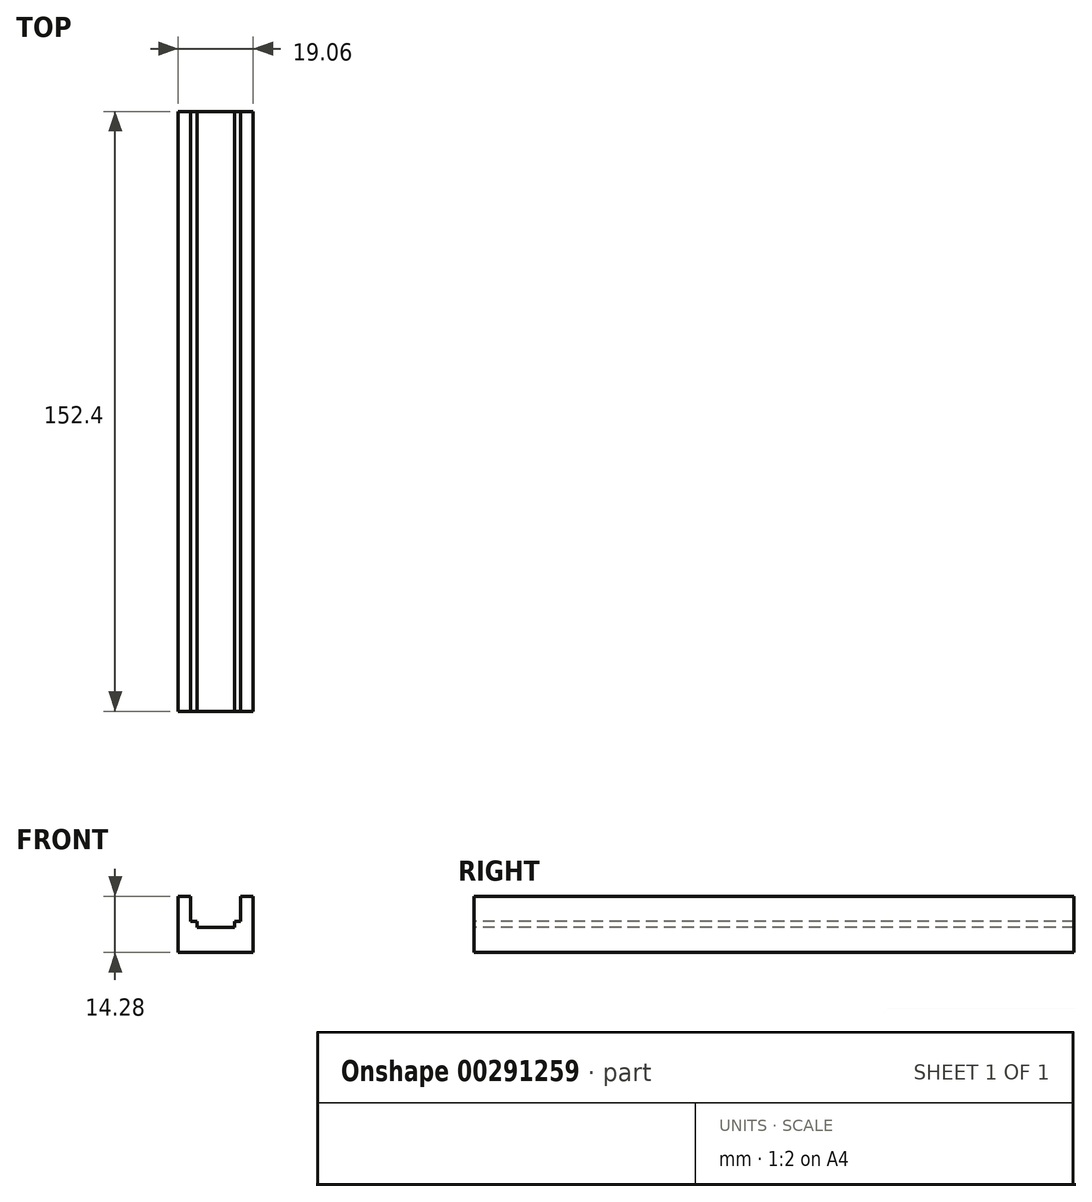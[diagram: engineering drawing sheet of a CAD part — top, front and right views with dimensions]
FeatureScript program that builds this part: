
annotation { "Feature Type Name" : "Feature", "Feature Type Description" : "" }
export const myFeature = defineFeature(function(context is Context, id is Id, definition is map)
    precondition{}
    {
        {
            var Q0;
            Q0=qCreatedBy(makeId("Front.planeOp"),FACE);
            var sketch = newSketch(context, id + "F0", { "sketchPlane" : qUnion([Q0])});
            skLineSegment(sketch, "E0", {"start": v(-4.76, 0) * mm, "end": v(4.76, 0) * mm});
            skLineSegment(sketch, "E1", {"start": v(4.76, 0) * mm, "end": v(4.76, 1.52) * mm});
            skLineSegment(sketch, "E2", {"start": v(4.76, 1.52) * mm, "end": v(6.35, 1.52) * mm});
            skLineSegment(sketch, "E3", {"start": v(6.35, 1.52) * mm, "end": v(6.35, 7.87) * mm});
            skLineSegment(sketch, "E4", {"start": v(6.35, 7.87) * mm, "end": v(9.53, 7.87) * mm});
            skLineSegment(sketch, "E5", {"start": v(9.53, 7.87) * mm, "end": v(9.53, -6.41) * mm});
            skLineSegment(sketch, "E6", {"start": v(9.53, -6.41) * mm, "end": v(-9.53, -6.41) * mm});
            skLineSegment(sketch, "E7", {"start": v(-9.53, -6.41) * mm, "end": v(-9.53, 7.87) * mm});
            skLineSegment(sketch, "E8", {"start": v(-9.53, 7.87) * mm, "end": v(-6.35, 7.87) * mm});
            skLineSegment(sketch, "E9", {"start": v(-6.35, 7.87) * mm, "end": v(-6.35, 1.52) * mm});
            skLineSegment(sketch, "E10", {"start": v(-6.35, 1.52) * mm, "end": v(-4.76, 1.52) * mm});
            skLineSegment(sketch, "E11", {"start": v(-4.76, 1.52) * mm, "end": v(-4.76, 0) * mm});
            skSolve(sketch);
        }
        {
            var Q0;
            Q0=makeQuery(id+"F0.imprint","IMPRINT",FACE,{"disambiguationData":[TD([[makeQuery(id+"F0.imprint","IMPRINT",EDGE,{"derivedFrom":sQuery(id+"F0.wireOp",EDGE,"E0")}),-1.0]])]});
            extrude(context, id + "F1", {"entities" : qUnion([Q0]), "oppositeDirection" : true, "depth" : 152.4 * mm});
        }
    });
